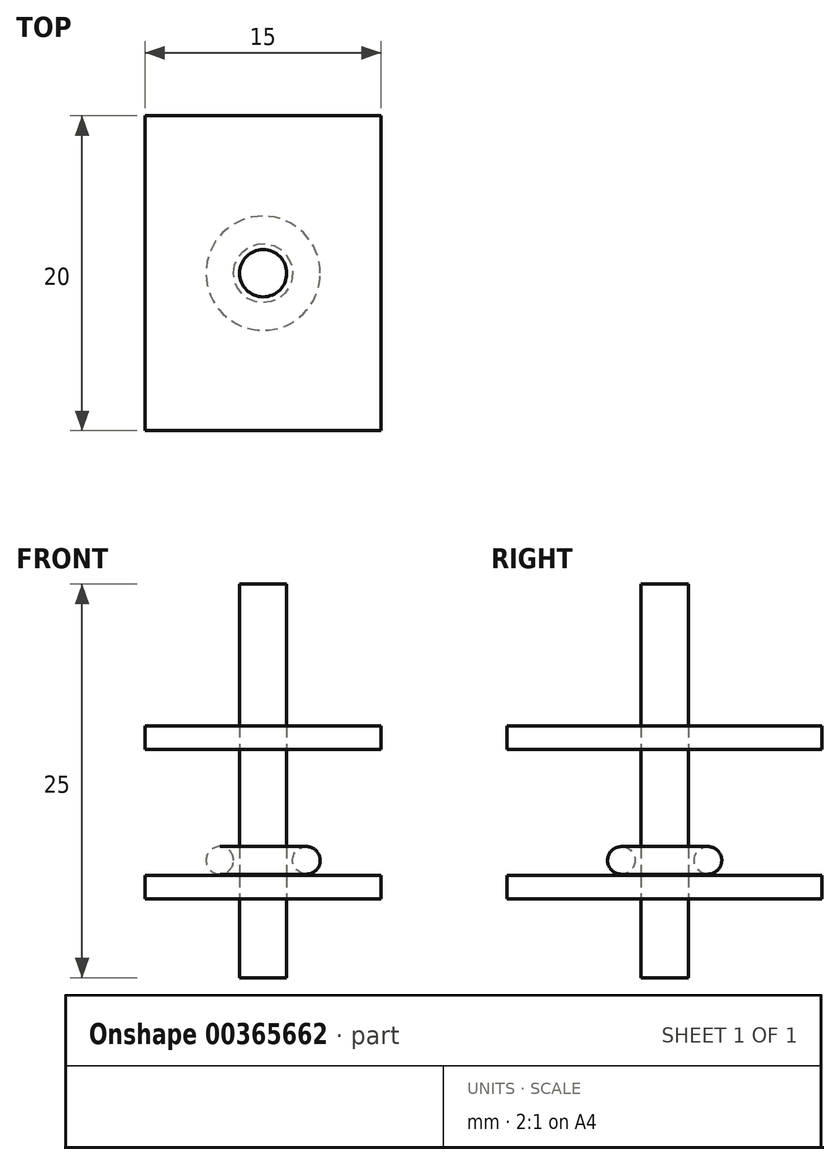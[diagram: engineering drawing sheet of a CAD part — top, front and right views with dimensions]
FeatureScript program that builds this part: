
annotation { "Feature Type Name" : "Feature", "Feature Type Description" : "" }
export const myFeature = defineFeature(function(context is Context, id is Id, definition is map)
    precondition{}
    {
        {
            var Q0;
            Q0=qCreatedBy(makeId("Top.planeOp"),FACE);
            var sketch = newSketch(context, id + "F0", { "sketchPlane" : qUnion([Q0])});
            skCircle(sketch, "E0", {"center": v(0, 0) * mm, "radius": 1.5 * mm});
            skSolve(sketch);
        }
        {
            var Q0;
            Q0=makeQuery(id+"F0.imprint","IMPRINT",FACE,{"disambiguationData":[TD([[makeQuery(id+"F0.imprint","IMPRINT",EDGE,{"derivedFrom":sQuery(id+"F0.wireOp",EDGE,"E0")}),1.0]])]});
            extrude(context, id + "F1", {"entities" : qUnion([Q0]), "depth" : 25 * mm});
        }
        {
            var Q0;
            Q0=qCreatedBy(makeId("Top.planeOp"),FACE);
            cPlane(context, id + "F2", {"entities" : qUnion([Q0]), "cplaneType" : CPlaneType.OFFSET, "offset" : 5 * mm, "width" : 150 * mm, "height" : 150 * mm});
        }
        {
            var Q0;
            Q0=qCreatedBy(id+"F2.planeOp",FACE);
            var sketch = newSketch(context, id + "F3", { "sketchPlane" : qUnion([Q0])});
            skLineSegment(sketch, "E1.bottom", {"start": v(7.5, -10) * mm, "end": v(-7.5, -10) * mm});
            skLineSegment(sketch, "E1.top", {"start": v(7.5, 10) * mm, "end": v(-7.5, 10) * mm});
            skLineSegment(sketch, "E1.left", {"start": v(7.5, -10) * mm, "end": v(7.5, 10) * mm});
            skLineSegment(sketch, "E1.right", {"start": v(-7.5, -10) * mm, "end": v(-7.5, 10) * mm});
            skPoint(sketch, "E1.middle", {"position": v(0, 0) * mm});
            skSolve(sketch);
        }
        {
            var Q0;
            Q0=makeQuery(id+"F3.imprint","IMPRINT",FACE,{"disambiguationData":[TD([[makeQuery(id+"F3.imprint","IMPRINT",EDGE,{"derivedFrom":sQuery(id+"F3.wireOp",EDGE,"E1.bottom")}),-1.0]])]});
            extrude(context, id + "F4", {"entities" : qUnion([Q0]), "depth" : 1.5 * mm});
        }
        {
            var Q0;
            Q0=makeQuery(id+"F4.opExtrude","CAP_FACE",FACE,{"disambiguationData":[OSD([sQuery(id+"F3.wireOp",EDGE,"E1.bottom"),sQuery(id+"F3.wireOp",EDGE,"E1.top"),sQuery(id+"F3.wireOp",EDGE,"E1.left"),sQuery(id+"F3.wireOp",EDGE,"E1.right")])],"isStart":false});
            cPlane(context, id + "F5", {"entities" : qUnion([Q0]), "cplaneType" : CPlaneType.OFFSET, "offset" : 8 * mm, "width" : 150 * mm, "height" : 150 * mm});
        }
        {
            var Q0;
            Q0=qCreatedBy(id+"F5.planeOp",FACE);
            var sketch = newSketch(context, id + "F6", { "sketchPlane" : qUnion([Q0])});
            skLineSegment(sketch, "E2.bottom", {"start": v(-7.5, -10) * mm, "end": v(7.5, -10) * mm});
            skLineSegment(sketch, "E2.top", {"start": v(-7.5, 10) * mm, "end": v(7.5, 10) * mm});
            skLineSegment(sketch, "E2.left", {"start": v(-7.5, -10) * mm, "end": v(-7.5, 10) * mm});
            skLineSegment(sketch, "E2.right", {"start": v(7.5, -10) * mm, "end": v(7.5, 10) * mm});
            skPoint(sketch, "E2.middle", {"position": v(0, 0) * mm});
            skSolve(sketch);
        }
        {
            var Q0;
            Q0=makeQuery(id+"F6.imprint","IMPRINT",FACE,{"disambiguationData":[TD([[makeQuery(id+"F6.imprint","IMPRINT",EDGE,{"derivedFrom":sQuery(id+"F6.wireOp",EDGE,"E2.bottom")}),1.0]])]});
            extrude(context, id + "F7", {"entities" : qUnion([Q0]), "depth" : 1.5 * mm});
        }
        {
            var Q0;
            Q0=qCreatedBy(makeId("Front.planeOp"),FACE);
            var sketch = newSketch(context, id + "F8", { "sketchPlane" : qUnion([Q0])});
            skCircle(sketch, "E3", {"center": v(-2.75, 7.45) * mm, "radius": 0.88 * mm});
            skLineSegment(sketch, "E4", {"start": v(0, -2.95) * mm, "end": v(0, 26.56) * mm});
            skSolve(sketch);
        }
        {
            var Q0;
            Q0=makeQuery(id+"F8.imprint","IMPRINT",FACE,{"disambiguationData":[TD([[makeQuery(id+"F8.imprint","IMPRINT",EDGE,{"derivedFrom":sQuery(id+"F8.wireOp",EDGE,"E3")}),1.0]])]});
            var Q1;
            Q1=sQuery(id+"F8.wireOp",EDGE,"E4");
            revolve(context, id + "F9", {"entities" : qUnion([Q0]), "axis" : qUnion([Q1]), "revolveType" : RevolveType.FULL});
        }
    });
